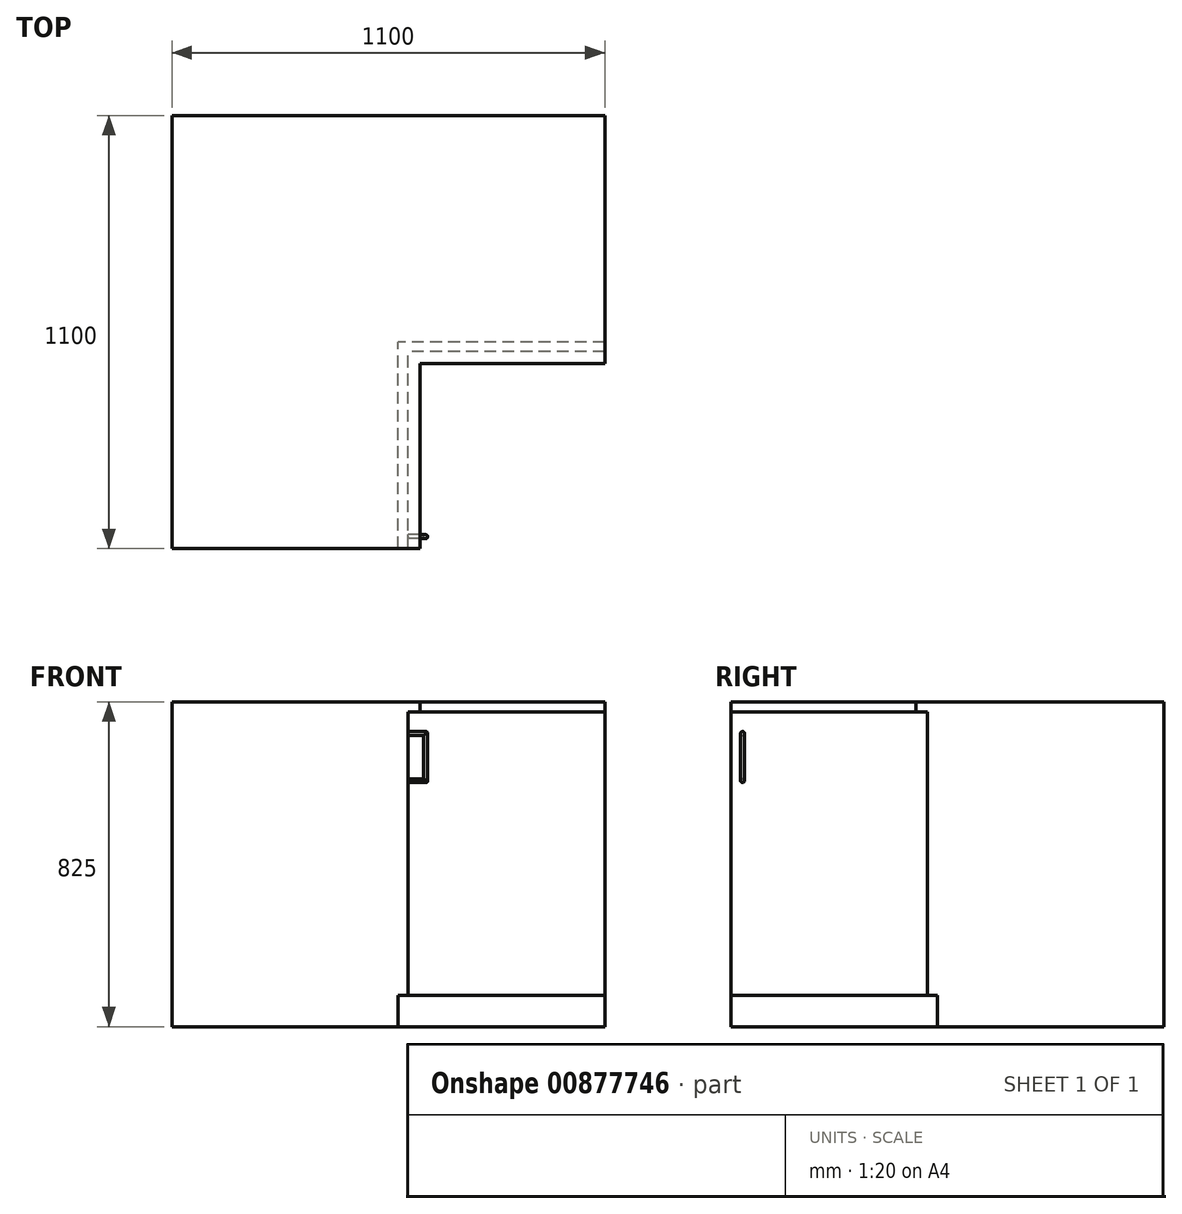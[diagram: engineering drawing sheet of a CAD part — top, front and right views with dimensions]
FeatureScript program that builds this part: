
annotation { "Feature Type Name" : "Feature", "Feature Type Description" : "" }
export const myFeature = defineFeature(function(context is Context, id is Id, definition is map)
    precondition{}
    {
        {
            var Q0;
            Q0=qCreatedBy(makeId("Top.planeOp"),FACE);
            var sketch = newSketch(context, id + "F0", { "sketchPlane" : qUnion([Q0])});
            skLineSegment(sketch, "E0.bottom", {"start": v(-300, 250) * mm, "end": v(300, 250) * mm});
            skLineSegment(sketch, "E0.top", {"start": v(-300, -250) * mm, "end": v(300, -250) * mm});
            skLineSegment(sketch, "E0.left", {"start": v(-300, 250) * mm, "end": v(-300, -250) * mm});
            skLineSegment(sketch, "E0.right", {"start": v(300, 250) * mm, "end": v(300, -250) * mm});
            skPoint(sketch, "E0.middle", {"position": v(0, 0) * mm});
            skSolve(sketch);
        }
        {
            var Q0;
            Q0=qSketchRegion(id+"F0",true);
            extrude(context, id + "F1", {"entities" : qUnion([Q0]), "depth" : 800 * mm, "offsetDistance" : 25 * mm});
        }
        {
            var Q0;
            Q0=makeQuery(id+"F1.opExtrude","SWEPT_FACE",FACE,{"disambiguationData":[OSD([sQuery(id+"F0.wireOp",EDGE,"E0.right")])]});
            var sketch = newSketch(context, id + "F2", { "sketchPlane" : qUnion([Q0])});
            skLineSegment(sketch, "E1.bottom", {"start": v(-250, 0) * mm, "end": v(250, 0) * mm});
            skLineSegment(sketch, "E1.top", {"start": v(-250, 80) * mm, "end": v(250, 80) * mm});
            skLineSegment(sketch, "E1.left", {"start": v(-250, 0) * mm, "end": v(-250, 80) * mm});
            skLineSegment(sketch, "E1.right", {"start": v(250, 0) * mm, "end": v(250, 80) * mm});
            skSolve(sketch);
        }
        {
            var Q0;
            Q0=qSketchRegion(id+"F2",true);
            extrude(context, id + "F3", {"entities" : qUnion([Q0]), "operationType" : NewBodyOperationType.REMOVE, "oppositeDirection" : true, "depth" : 25 * mm, "offsetDistance" : 25 * mm});
        }
        {
            var Q0;
            Q0=makeQuery(id+"F1.opExtrude","SWEPT_FACE",FACE,{"disambiguationData":[OSD([sQuery(id+"F0.wireOp",EDGE,"E0.right")])]});
            var sketch = newSketch(context, id + "F4", { "sketchPlane" : qUnion([Q0])});
            skLineSegment(sketch, "E2.bottom", {"start": v(-220, 750) * mm, "end": v(-220, 750) * mm});
            skLineSegment(sketch, "E2.top", {"start": v(-220, 620) * mm, "end": v(-220, 620) * mm});
            skLineSegment(sketch, "E2.left", {"start": v(-225, 745) * mm, "end": v(-225, 625) * mm});
            skLineSegment(sketch, "E2.right", {"start": v(-215, 745) * mm, "end": v(-215, 625) * mm});
            skPoint(sketch, "E3.visualSharp", {"position": v(-215, 750) * mm});
            skArc(sketch, "E3.filletArc", {"start": v(-215, 745) * mm, "mid": v(-216.46, 748.54) * mm, "end": v(-220, 750) * mm});
            skPoint(sketch, "E4.visualSharp", {"position": v(-215, 620) * mm});
            skArc(sketch, "E4.filletArc", {"start": v(-220, 620) * mm, "mid": v(-216.46, 621.46) * mm, "end": v(-215, 625) * mm});
            skPoint(sketch, "E5.visualSharp", {"position": v(-225, 620) * mm});
            skArc(sketch, "E5.filletArc", {"start": v(-225, 625) * mm, "mid": v(-223.54, 621.46) * mm, "end": v(-220, 620) * mm});
            skPoint(sketch, "E6.visualSharp", {"position": v(-225, 750) * mm});
            skArc(sketch, "E6.filletArc", {"start": v(-220, 750) * mm, "mid": v(-223.54, 748.54) * mm, "end": v(-225, 745) * mm});
            skSolve(sketch);
        }
        {
            var Q0;
            Q0=qSketchRegion(id+"F4",true);
            extrude(context, id + "F5", {"entities" : qUnion([Q0]), "operationType" : NewBodyOperationType.ADD, "depth" : 50 * mm, "offsetDistance" : 25 * mm});
        }
        {
            var Q0;
            Q0=makeQuery(id+"F5.opExtrude","CAP_FACE",FACE,{"disambiguationData":[OSD([sQuery(id+"F4.wireOp",EDGE,"E2.left"),sQuery(id+"F4.wireOp",EDGE,"E2.right"),sQuery(id+"F4.wireOp",EDGE,"E3.filletArc"),sQuery(id+"F4.wireOp",EDGE,"E4.filletArc"),sQuery(id+"F4.wireOp",EDGE,"E5.filletArc"),sQuery(id+"F4.wireOp",EDGE,"E6.filletArc")])],"isStart":false});
            fillet(context, id + "F6", {"entities" : qUnion([Q0]), "radius" : 5 * mm, "tangentPropagation" : true, "allowEdgeOverflow" : false});
        }
        {
            var Q0;
            Q0=makeQuery(id+"F5.opExtrude","SWEPT_FACE",FACE,{"disambiguationData":[OSD([sQuery(id+"F4.wireOp",EDGE,"E2.right")])]});
            var sketch = newSketch(context, id + "F7", { "sketchPlane" : qUnion([Q0])});
            skLineSegment(sketch, "E7.bottom", {"start": v(-340, 740) * mm, "end": v(-300, 740) * mm});
            skLineSegment(sketch, "E7.top", {"start": v(-340, 630) * mm, "end": v(-300, 630) * mm});
            skLineSegment(sketch, "E7.left", {"start": v(-340, 740) * mm, "end": v(-340, 630) * mm});
            skLineSegment(sketch, "E7.right", {"start": v(-300, 740) * mm, "end": v(-300, 630) * mm});
            skSolve(sketch);
        }
        {
            var Q0;
            Q0=makeQuery(id+"F7.imprint","IMPRINT",FACE,{"disambiguationData":[TD([[makeQuery(id+"F7.imprint","IMPRINT",EDGE,{"derivedFrom":sQuery(id+"F7.wireOp",EDGE,"E7.bottom")}),-1.0]])]});
            extrude(context, id + "F8", {"entities" : qUnion([Q0]), "operationType" : NewBodyOperationType.REMOVE, "oppositeDirection" : true, "depth" : 25 * mm, "offsetDistance" : 25 * mm});
        }
        {
            var Q0;
            Q0=makeQuery(id+"F8.boolean.opBoolean","COPY",EDGE,{"derivedFrom":makeQuery(id+"F8.opExtrude","CAP_EDGE",EDGE,{"disambiguationData":[OSD([sQuery(id+"F7.wireOp",EDGE,"E7.bottom")])],"isStart":true})});
            var Q1;
            Q1=makeQuery(id+"F8.boolean.opBoolean","COPY",EDGE,{"derivedFrom":makeQuery(id+"F8.opExtrude","CAP_EDGE",EDGE,{"disambiguationData":[OSD([sQuery(id+"F7.wireOp",EDGE,"E7.left")])],"isStart":true})});
            var Q2;
            Q2=makeQuery(id+"F8.boolean.opBoolean","COPY",EDGE,{"derivedFrom":makeQuery(id+"F8.opExtrude","CAP_EDGE",EDGE,{"disambiguationData":[OSD([sQuery(id+"F7.wireOp",EDGE,"E7.top")])],"isStart":true})});
            var Q3;
            Q3=makeQuery(id+"F8.boolean.opBoolean","INTERSECT",EDGE,{"derivedFrom":[makeQuery(id+"F5.opExtrude","SWEPT_FACE",FACE,{"disambiguationData":[OSD([sQuery(id+"F4.wireOp",EDGE,"E2.left")])]}),makeQuery(id+"F8.opExtrude","SWEPT_FACE",FACE,{"disambiguationData":[OSD([sQuery(id+"F7.wireOp",EDGE,"E7.bottom")])]})]});
            var Q4;
            Q4=makeQuery(id+"F8.boolean.opBoolean","INTERSECT",EDGE,{"derivedFrom":[makeQuery(id+"F5.opExtrude","SWEPT_FACE",FACE,{"disambiguationData":[OSD([sQuery(id+"F4.wireOp",EDGE,"E2.left")])]}),makeQuery(id+"F8.opExtrude","SWEPT_FACE",FACE,{"disambiguationData":[OSD([sQuery(id+"F7.wireOp",EDGE,"E7.left")])]})]});
            var Q5;
            Q5=makeQuery(id+"F8.boolean.opBoolean","INTERSECT",EDGE,{"derivedFrom":[makeQuery(id+"F5.opExtrude","SWEPT_FACE",FACE,{"disambiguationData":[OSD([sQuery(id+"F4.wireOp",EDGE,"E2.left")])]}),makeQuery(id+"F8.opExtrude","SWEPT_FACE",FACE,{"disambiguationData":[OSD([sQuery(id+"F7.wireOp",EDGE,"E7.top")])]})]});
            fillet(context, id + "F9", {"entities" : qUnion([Q0, Q1, Q2, Q3, Q4, Q5]), "radius" : 5 * mm, "tangentPropagation" : true, "allowEdgeOverflow" : false});
        }
        {
            var Q0;
            Q0=makeQuery(id+"F1.opExtrude","CAP_FACE",FACE,{"disambiguationData":[OSD([sQuery(id+"F0.wireOp",EDGE,"E0.bottom"),sQuery(id+"F0.wireOp",EDGE,"E0.top"),sQuery(id+"F0.wireOp",EDGE,"E0.left"),sQuery(id+"F0.wireOp",EDGE,"E0.right")])],"isStart":false});
            var sketch = newSketch(context, id + "F10", { "sketchPlane" : qUnion([Q0])});
            skLineSegment(sketch, "E8.bottom", {"start": v(-300, -250) * mm, "end": v(330, -250) * mm});
            skLineSegment(sketch, "E8.top", {"start": v(-300, 250) * mm, "end": v(330, 250) * mm});
            skLineSegment(sketch, "E8.left", {"start": v(-300, -250) * mm, "end": v(-300, 250) * mm});
            skLineSegment(sketch, "E8.right", {"start": v(330, -250) * mm, "end": v(330, 250) * mm});
            skSolve(sketch);
        }
        {
            var Q0;
            Q0=qSketchRegion(id+"F10",true);
            extrude(context, id + "F11", {"entities" : qUnion([Q0]), "operationType" : NewBodyOperationType.ADD, "depth" : 25 * mm, "offsetDistance" : 25 * mm});
        }
        {
            var Q0;
            Q0=makeQuery(id+"F11.boolean.opBoolean","MERGE",FACE,{"derivedFrom":[makeQuery(id+"F1.opExtrude","SWEPT_FACE",FACE,{"disambiguationData":[OSD([sQuery(id+"F0.wireOp",EDGE,"E0.bottom")])]}),makeQuery(id+"F11.opExtrude","SWEPT_FACE",FACE,{"disambiguationData":[OSD([sQuery(id+"F10.wireOp",EDGE,"E8.top")])]})]});
            extrude(context, id + "F12", {"entities" : qUnion([Q0]), "operationType" : NewBodyOperationType.ADD, "depth" : 600 * mm, "offsetDistance" : 25 * mm});
        }
        {
            var Q0;
            {var subQ0=sQuery(id+"F0.wireOp",EDGE,"E0.right");Q0=makeQuery(id+"F12.boolean.opBoolean","MERGE",FACE,{"derivedFrom":[makeQuery(id+"F8.boolean.opBoolean","MERGE",FACE,{"derivedFrom":[makeQuery(id+"F1.opExtrude","SWEPT_FACE",FACE,{"disambiguationData":[OSD([subQ0])]})],"fromTools":[makeQuery(id+"F8.opExtrude","SWEPT_FACE",FACE,{"disambiguationData":[OSD([sQuery(id+"F7.wireOp",EDGE,"E7.right")])]})]}),makeQuery(id+"F12.opExtrude","SWEPT_FACE",FACE,{"disambiguationData":[OSD([sQuery(id+"F0.wireOp",EDGE,"E0.bottom"),subQ0])]})]});}
            var sketch = newSketch(context, id + "F13", { "sketchPlane" : qUnion([Q0])});
            skLineSegment(sketch, "E9.top", {"start": v(850, 800) * mm, "end": v(250, 800) * mm});
            skLineSegment(sketch, "E9.left", {"start": v(850, 0) * mm, "end": v(850, 800) * mm});
            skLineSegment(sketch, "E10.bottom", {"start": v(850, 0) * mm, "end": v(250, 0) * mm});
            skLineSegment(sketch, "E11", {"start": v(250, 800) * mm, "end": v(250, 0) * mm});
            skSolve(sketch);
        }
        {
            var Q0;
            Q0 = qSketchRegion(id + "F13", true);
            extrude(context, id + "F14", {"entities" : qUnion([Q0]), "operationType" : NewBodyOperationType.ADD, "depth" : 500 * mm, "offsetDistance" : 25 * mm});
        }
        {
            var Q0;
            {var subQ0=sQuery(id+"F10.wireOp",EDGE,"E8.right");Q0=makeQuery(id+"F12.boolean.opBoolean","MERGE",FACE,{"derivedFrom":[makeQuery(id+"F11.opExtrude","SWEPT_FACE",FACE,{"disambiguationData":[OSD([subQ0])]}),makeQuery(id+"F12.opExtrude","SWEPT_FACE",FACE,{"disambiguationData":[OSD([sQuery(id+"F10.wireOp",EDGE,"E8.top"),subQ0])]})]});}
            var sketch = newSketch(context, id + "F15", { "sketchPlane" : qUnion([Q0])});
            skLineSegment(sketch, "E12.bottom", {"start": v(850, 825) * mm, "end": v(220, 825) * mm});
            skLineSegment(sketch, "E12.top", {"start": v(850, 800) * mm, "end": v(220, 800) * mm});
            skLineSegment(sketch, "E12.left", {"start": v(850, 825) * mm, "end": v(850, 800) * mm});
            skLineSegment(sketch, "E12.right", {"start": v(220, 825) * mm, "end": v(220, 800) * mm});
            skSolve(sketch);
        }
        {
            var Q0;
            Q0 = qSketchRegion(id + "F15", true);
            extrude(context, id + "F16", {"entities" : qUnion([Q0]), "operationType" : NewBodyOperationType.ADD, "depth" : 470 * mm, "offsetDistance" : 25 * mm});
        }
        {
            var Q0;
            Q0=makeQuery(id+"F14.opExtrude","SWEPT_FACE",FACE,{"disambiguationData":[OSD([sQuery(id+"F13.wireOp",EDGE,"E11")])]});
            var sketch = newSketch(context, id + "F17", { "sketchPlane" : qUnion([Q0])});
            skLineSegment(sketch, "E13.bottom", {"start": v(800, 0) * mm, "end": v(300, 0) * mm});
            skLineSegment(sketch, "E13.top", {"start": v(800, 80) * mm, "end": v(300, 80) * mm});
            skLineSegment(sketch, "E13.left", {"start": v(800, 0) * mm, "end": v(800, 80) * mm});
            skLineSegment(sketch, "E13.right", {"start": v(300, 0) * mm, "end": v(300, 80) * mm});
            skSolve(sketch);
        }
        {
            var Q0;
            Q0 = qSketchRegion(id + "F17", true);
            extrude(context, id + "F18", {"entities" : qUnion([Q0]), "operationType" : NewBodyOperationType.REMOVE, "oppositeDirection" : true, "depth" : 25 * mm, "offsetDistance" : 25 * mm});
        }
        {
            var Q0;
            Q0=makeQuery(id+"F14.opExtrude","CAP_FACE",FACE,{"disambiguationData":[OSD([sQuery(id+"F13.wireOp",EDGE,"E10.bottom"),sQuery(id+"F13.wireOp",EDGE,"E9.top"),sQuery(id+"F13.wireOp",EDGE,"E9.left"),sQuery(id+"F13.wireOp",EDGE,"E11")])],"isStart":true});
            var sketch = newSketch(context, id + "F19", { "sketchPlane" : qUnion([Q0])});
            skLineSegment(sketch, "E14.bottom", {"start": v(-850, 0) * mm, "end": v(-275, 0) * mm});
            skLineSegment(sketch, "E14.top", {"start": v(-850, 80) * mm, "end": v(-275, 80) * mm});
            skLineSegment(sketch, "E14.left", {"start": v(-850, 0) * mm, "end": v(-850, 80) * mm});
            skLineSegment(sketch, "E14.right", {"start": v(-275, 0) * mm, "end": v(-275, 80) * mm});
            skSolve(sketch);
        }
        {
            var Q0;
            Q0 = qSketchRegion(id + "F19", true);
            extrude(context, id + "F20", {"entities" : qUnion([Q0]), "operationType" : NewBodyOperationType.ADD, "depth" : 25 * mm, "offsetDistance" : 25 * mm});
        }
    });
